# Revit family: STH20971BR_27_STH20971PTO_27
name_source: partatom
category: Luminárias
units: mm (PartAtom-declared; Revit-internal decimal feet)

## family parameters
Compartilhado = Não
Corte com vazios quando carregada = Não
Cota do conector redondo = Utilizar diâmetro
Fonte luminosa = Sim
Hospedeiro = Forro
Manter orientação da anotação = Não
Número OmniClass = 23.80.70.11
Ponto de cálculo do ambiente = Não
Sempre na vertical = Sim
Tipo de parte = Normal
Título OmniClass = Luminaries for Internal Lighting

## types (2) — shared parameters
Altura = 0.04 m
Arquivo de rede fotométrica = STELLA - STH20971BR-27 - ARCHI - PERFIL DE SOBREPOR PLANO 24V.ies
Comprimento = 1.01 m
Dimerização = Não dimerizável
Fabricante = Stella
Filtro de cor = 16777215
Grau de proteção (IP) = IP20
IRC (Índice de reprodução de cores) = >93 (R9 >60)
Largura = 0.04 m
Luminoso = Luminoso - 2700K
Modelo = Archi
Potência = 28 W
Temperatura da cor (K) = 2700 K
Tensão Elétrica = 24V
Troca de temperatura da cor de lâmpada com esmaecimento = <Nenhum>
URL = https://stella.com.br
Ângulo de Abertura = 110°
Ângulo de inclinação = 90.00°
zero-valued in all types: Elevação padrão

## per-type parameters (varying)
| type | Estrutura | Fluxo Luminoso | Referência |
| STH20971BR/27 - BRANCO - 1m - 2700K - 960lm - 110° | Al - Branco | 960 lm | STH20971BR/27 - BRANCO - 1m |
| STH20971PTO/27 - PRETO - 1m - 2700K - 650lm - 110° | Al - Preto | 650 lm | STH20971PTO/27 - PRETO - 1m |
